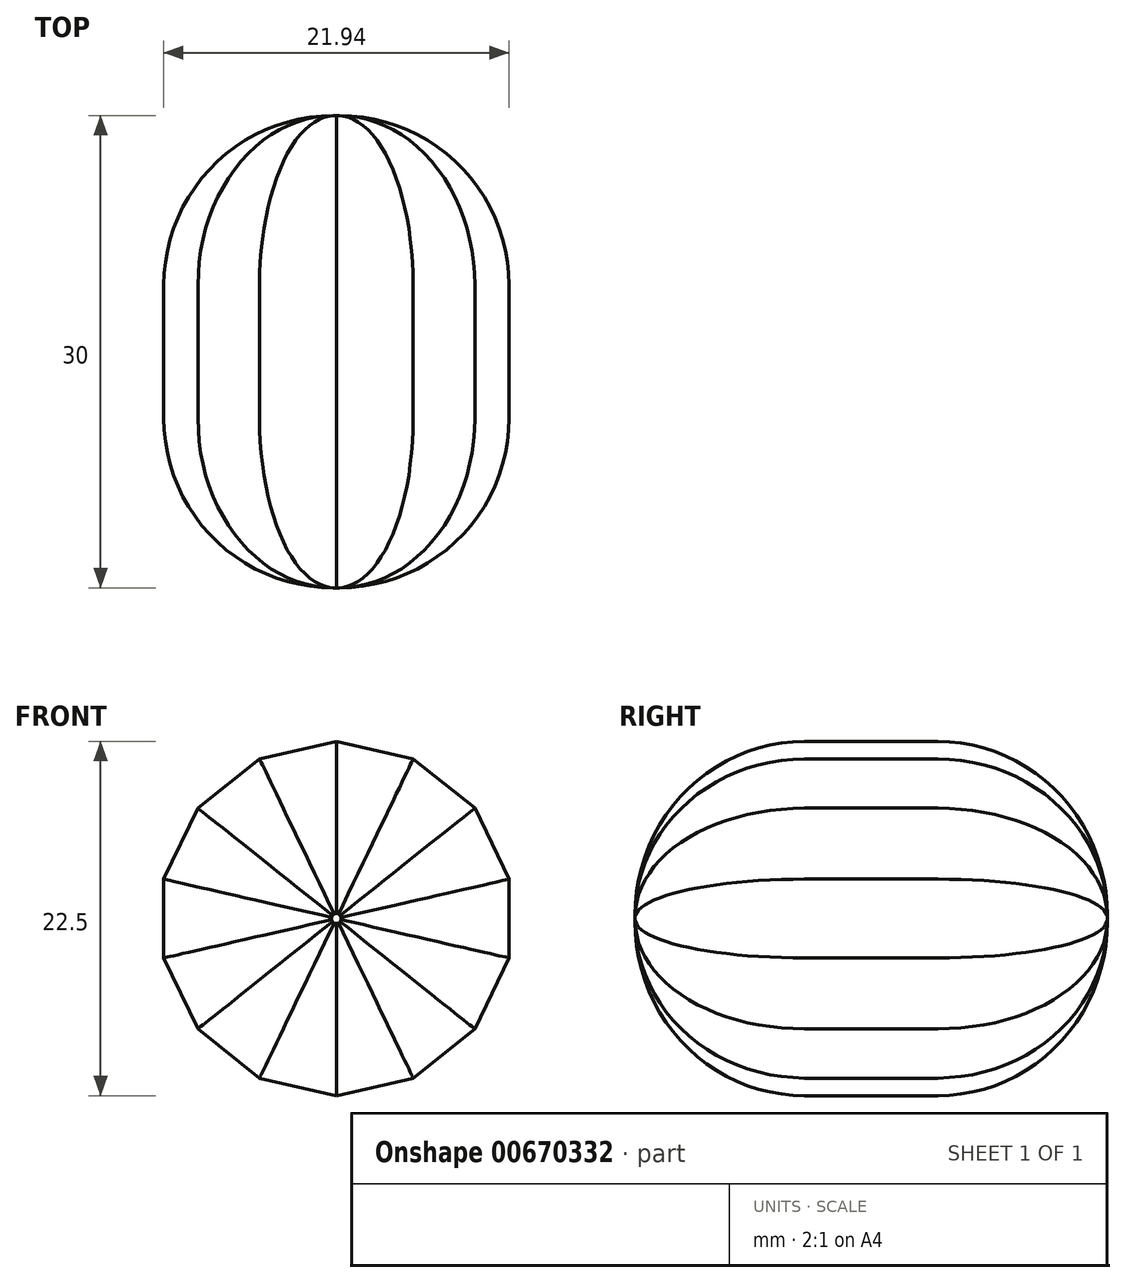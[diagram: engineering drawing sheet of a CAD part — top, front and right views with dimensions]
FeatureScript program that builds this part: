
annotation { "Feature Type Name" : "Feature", "Feature Type Description" : "" }
export const myFeature = defineFeature(function(context is Context, id is Id, definition is map)
    precondition{}
    {
        {
            var Q0;
            Q0=qCreatedBy(makeId("Front.planeOp"),FACE);
            var sketch = newSketch(context, id + "F0", { "sketchPlane" : qUnion([Q0])});
            skCircle(sketch, "E0.cCircle", {"center": v(0, 0) * mm, "radius": 10.97 * mm, "construction": true});
            skLineSegment(sketch, "E0.0", {"start": v(10.97, 2.5) * mm, "end": v(10.97, -2.5) * mm});
            skLineSegment(sketch, "E0.1", {"start": v(10.97, -2.5) * mm, "end": v(8.8, -7.01) * mm});
            skLineSegment(sketch, "E0.2", {"start": v(8.8, -7.01) * mm, "end": v(4.88, -10.14) * mm});
            skLineSegment(sketch, "E0.3", {"start": v(4.88, -10.14) * mm, "end": v(0, -11.25) * mm});
            skLineSegment(sketch, "E0.4", {"start": v(0, -11.25) * mm, "end": v(-4.88, -10.14) * mm});
            skLineSegment(sketch, "E0.5", {"start": v(-4.88, -10.14) * mm, "end": v(-8.8, -7.01) * mm});
            skLineSegment(sketch, "E0.6", {"start": v(-8.8, -7.01) * mm, "end": v(-10.97, -2.5) * mm});
            skLineSegment(sketch, "E0.7", {"start": v(-10.97, -2.5) * mm, "end": v(-10.97, 2.5) * mm});
            skLineSegment(sketch, "E0.8", {"start": v(-10.97, 2.5) * mm, "end": v(-8.8, 7.01) * mm});
            skLineSegment(sketch, "E0.9", {"start": v(-8.8, 7.01) * mm, "end": v(-4.88, 10.14) * mm});
            skLineSegment(sketch, "E0.10", {"start": v(-4.88, 10.14) * mm, "end": v(0, 11.25) * mm});
            skLineSegment(sketch, "E0.11", {"start": v(0, 11.25) * mm, "end": v(4.88, 10.14) * mm});
            skLineSegment(sketch, "E0.12", {"start": v(4.88, 10.14) * mm, "end": v(8.8, 7.01) * mm});
            skLineSegment(sketch, "E0.13", {"start": v(8.8, 7.01) * mm, "end": v(10.97, 2.5) * mm});
            skPoint(sketch, "E0.0.midPoint", {"position": v(10.97, 0) * mm});
            skSolve(sketch);
        }
        {
            var Q0;
            Q0 = qSketchRegion(id + "F0", true);
            extrude(context, id + "F1", {"entities" : qUnion([Q0]), "depth" : 15 * mm, "offsetDistance" : 25 * mm, "hasSecondDirection" : true, "secondDirectionOppositeDirection" : true, "secondDirectionDepth" : 15 * mm});
        }
        {
            var Q0;
            Q0=makeQuery(id+"F1.opExtrude","CAP_FACE",FACE,{"disambiguationData":[OSD([sQuery(id+"F0.wireOp",EDGE,"E0.0"),sQuery(id+"F0.wireOp",EDGE,"E0.1"),sQuery(id+"F0.wireOp",EDGE,"E0.2"),sQuery(id+"F0.wireOp",EDGE,"E0.3"),sQuery(id+"F0.wireOp",EDGE,"E0.4"),sQuery(id+"F0.wireOp",EDGE,"E0.5"),sQuery(id+"F0.wireOp",EDGE,"E0.6"),sQuery(id+"F0.wireOp",EDGE,"E0.7"),sQuery(id+"F0.wireOp",EDGE,"E0.8"),sQuery(id+"F0.wireOp",EDGE,"E0.9"),sQuery(id+"F0.wireOp",EDGE,"E0.10"),sQuery(id+"F0.wireOp",EDGE,"E0.11"),sQuery(id+"F0.wireOp",EDGE,"E0.12"),sQuery(id+"F0.wireOp",EDGE,"E0.13")])],"isStart":false});
            var Q1;
            Q1=makeQuery(id+"F1.opExtrude","CAP_FACE",FACE,{"disambiguationData":[OSD([sQuery(id+"F0.wireOp",EDGE,"E0.0"),sQuery(id+"F0.wireOp",EDGE,"E0.1"),sQuery(id+"F0.wireOp",EDGE,"E0.2"),sQuery(id+"F0.wireOp",EDGE,"E0.3"),sQuery(id+"F0.wireOp",EDGE,"E0.4"),sQuery(id+"F0.wireOp",EDGE,"E0.5"),sQuery(id+"F0.wireOp",EDGE,"E0.6"),sQuery(id+"F0.wireOp",EDGE,"E0.7"),sQuery(id+"F0.wireOp",EDGE,"E0.8"),sQuery(id+"F0.wireOp",EDGE,"E0.9"),sQuery(id+"F0.wireOp",EDGE,"E0.10"),sQuery(id+"F0.wireOp",EDGE,"E0.11"),sQuery(id+"F0.wireOp",EDGE,"E0.12"),sQuery(id+"F0.wireOp",EDGE,"E0.13")])],"isStart":true});
            fillet(context, id + "F2", {"entities" : qUnion([Q0, Q1]), "radius" : 10.75 * mm, "tangentPropagation" : true, "allowEdgeOverflow" : false});
        }
    });
